# Revit family: 1224xxx Atelier Desk
name_source: partatom
category: Lighting Fixtures
revit_build: Autodesk Revit 2018 (Build: 20170223_1515(x64)
units: mm (PartAtom-declared; Revit-internal decimal feet)

## family parameters
Always vertical = Yes
Cut with Voids When Loaded = No
Light Source = No
OmniClass Number = 23.80.70.00
OmniClass Title = Lighting
Part Type = Normal
Room Calculation Point = No
Round Connector Dimension = Use Diameter
Shared = No
Work Plane-Based = No

## types (2) — shared parameters
Manufacturer URL - Europe and Rest of World = www.astrolighting.com
Manufacturer URL - North America = us.astrolighting.com

## per-type parameters (varying)
| type | Dimmable | Dimming Method | Driver Included | Driver Required | Efficacy (lm/W) | Electrical Class | Lamp | Length of Cable Supplied | Light Source Fixed | Main Finish | Main Material | Power (W) | Product CCT | Product CRI | Product Dimensions (MM) | Product Name | Product SKU | Product Weight (KG) | Wattage Comments |
| CE | Yes | Lamp Dependent | Not Applicable | Not Applicable | Lamp Dependent | Class II | E27 LED - 12W Max | 2.8m | Yes | Matt White | Metal - Aluminium | Lamp Dependent | Lamp Dependent | Lamp Dependent | 500x200x160 | Atelier Desk | 1224xxx | 2.47 | Not Applicable |
| ETL |  |  |  |  |  |  |  |  |  |  |  |  | 2700K / 3000K | 80 / 90 |  |  | 1234567 |  |  |

## geometry (parser evidence)
native form markers: Sweep x2
no freeform markers — native parametric forms only
